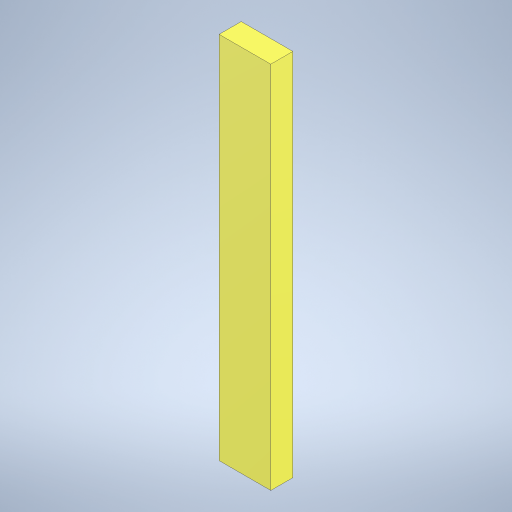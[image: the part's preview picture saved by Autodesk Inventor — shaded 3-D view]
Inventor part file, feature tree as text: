
AUTODESK INVENTOR PART (.ipt)
format: ipt  version: 2023 (Build 270158000, 158)  size: 227,328 bytes
history: native  units: in
note: dims shown in document units (in); Inventor stores cm internally (conversion verified against a paired STEP export)
features: extrude x1, sketch x1
ambient origin geometry x8: Origin, YZ Plane, XZ Plane, XY Plane, X Axis, Y Axis, Z Axis, Center Point
bodies: Solid1 (feature_tree)
feature tree (2):
  extrude  "Extrusion1"  Depth=0.28in
  sketch  "Sketch1"  dims[d0=2.0in d1=0.28in d2=0.12in d3=0.0in]
